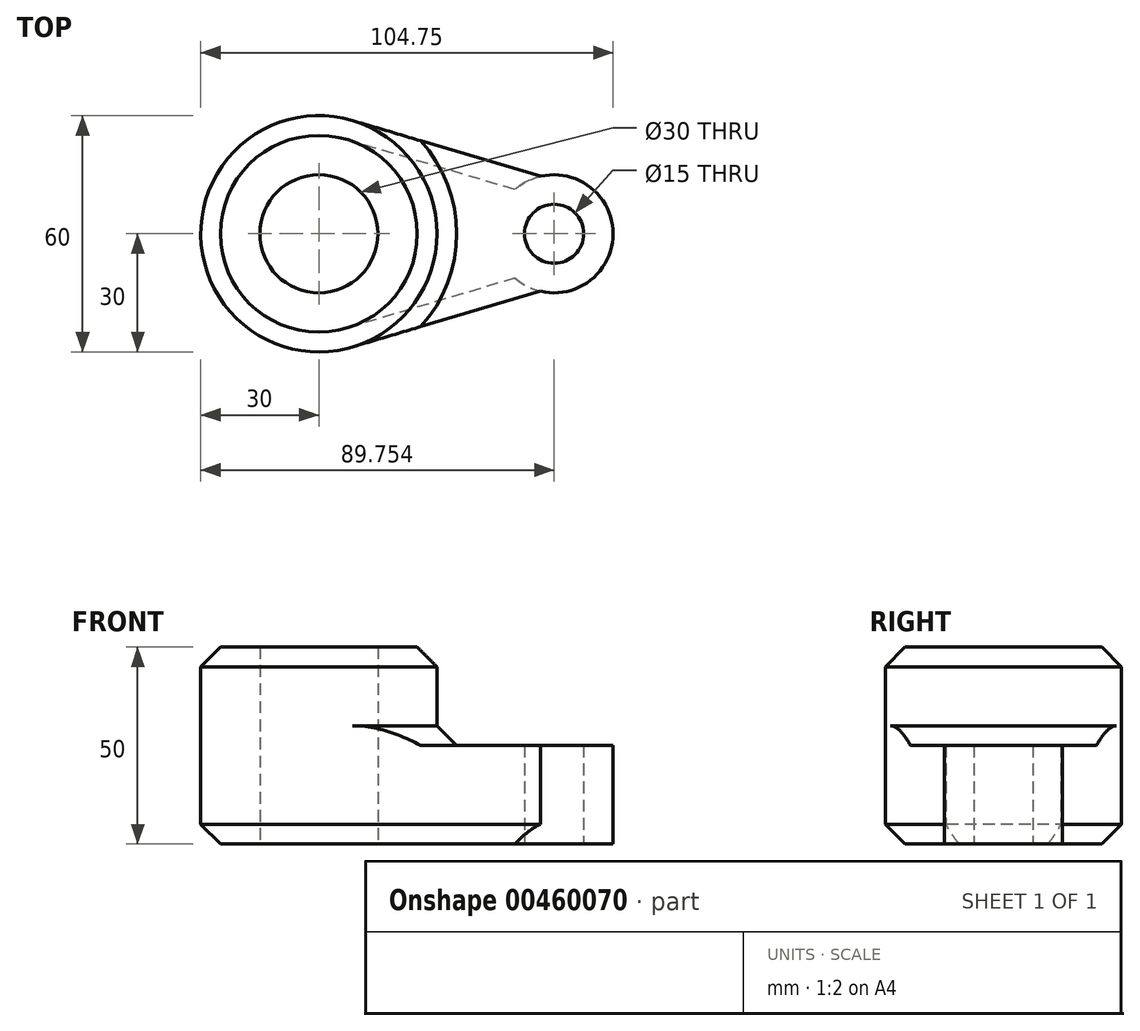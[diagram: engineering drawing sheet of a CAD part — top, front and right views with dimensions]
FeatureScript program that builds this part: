
annotation { "Feature Type Name" : "Feature", "Feature Type Description" : "" }
export const myFeature = defineFeature(function(context is Context, id is Id, definition is map)
    precondition{}
    {
        {
            var Q0;
            Q0=qCreatedBy(makeId("Top.planeOp"),FACE);
            var sketch = newSketch(context, id + "F0", { "sketchPlane" : qUnion([Q0])});
            skCircle(sketch, "E0", {"center": v(0, 0) * mm, "radius": 30 * mm});
            skCircle(sketch, "E1", {"center": v(59.75, 0) * mm, "radius": 15 * mm});
            skPoint(sketch, "E2", {"position": v(-114.36, 38.73) * mm});
            skLineSegment(sketch, "E3", {"start": v(8.5, 28.77) * mm, "end": v(56.37, 14.61) * mm});
            skLineSegment(sketch, "E4", {"start": v(8.54, -28.76) * mm, "end": v(56.27, -14.59) * mm});
            skCircle(sketch, "E5", {"center": v(0, 0) * mm, "radius": 15 * mm});
            skCircle(sketch, "E6", {"center": v(59.75, 0) * mm, "radius": 7.5 * mm});
            skSolve(sketch);
        }
        {
            var Q0;
            Q0=makeQuery(id+"F0.imprint","IMPRINT",FACE,{"disambiguationData":[TD([[makeQuery(id+"F0.imprint","IMPRINT",EDGE,{"derivedFrom":sQuery(id+"F0.wireOp",EDGE,"E5")}),-1.0]])]});
            var Q1;
            {var subQ0=sQuery(id+"F0.wireOp",EDGE,"E3");Q1=makeQuery(id+"F0.imprint","IMPRINT",FACE,{"disambiguationData":[TD([[makeQuery(id+"F0.imprint","IMPRINT",EDGE,{"derivedFrom":subQ0}),-1.0]])]});}
            var Q2;
            Q2=makeQuery(id+"F0.imprint","IMPRINT",FACE,{"disambiguationData":[TD([[makeQuery(id+"F0.imprint","IMPRINT",EDGE,{"derivedFrom":sQuery(id+"F0.wireOp",EDGE,"E6")}),-1.0]])]});
            extrude(context, id + "F1", {"entities" : qUnion([Q0, Q1, Q2]), "depth" : 25 * mm});
        }
        {
            var Q0;
            Q0=makeQuery(id+"F0.imprint","IMPRINT",FACE,{"disambiguationData":[TD([[makeQuery(id+"F0.imprint","IMPRINT",EDGE,{"derivedFrom":sQuery(id+"F0.wireOp",EDGE,"E5")}),-1.0]])]});
            extrude(context, id + "F2", {"entities" : qUnion([Q0]), "operationType" : NewBodyOperationType.ADD, "depth" : 50 * mm});
        }
        {
            var Q0;
            Q0=makeQuery(id+"F2.opExtrude","CAP_EDGE",EDGE,{"disambiguationData":[OSD([sQuery(id+"F0.wireOp",EDGE,"E0")])],"isStart":false});
            var Q1;
            {var subQ0=sQuery(id+"F0.wireOp",EDGE,"E0");Q1=makeQuery(id+"F2.boolean.opBoolean","MERGE",FACE,{"derivedFrom":[makeQuery(id+"F1.opExtrude","SWEPT_FACE",FACE,{"disambiguationData":[OSD([subQ0])]}),makeQuery(id+"F2.opExtrude","SWEPT_FACE",FACE,{"disambiguationData":[OSD([subQ0])]})]});}
            chamfer(context, id + "F3", {"entities" : qUnion([Q0, Q1]), "width" : 5 * mm, "tangentPropagation" : true});
        }
    });
